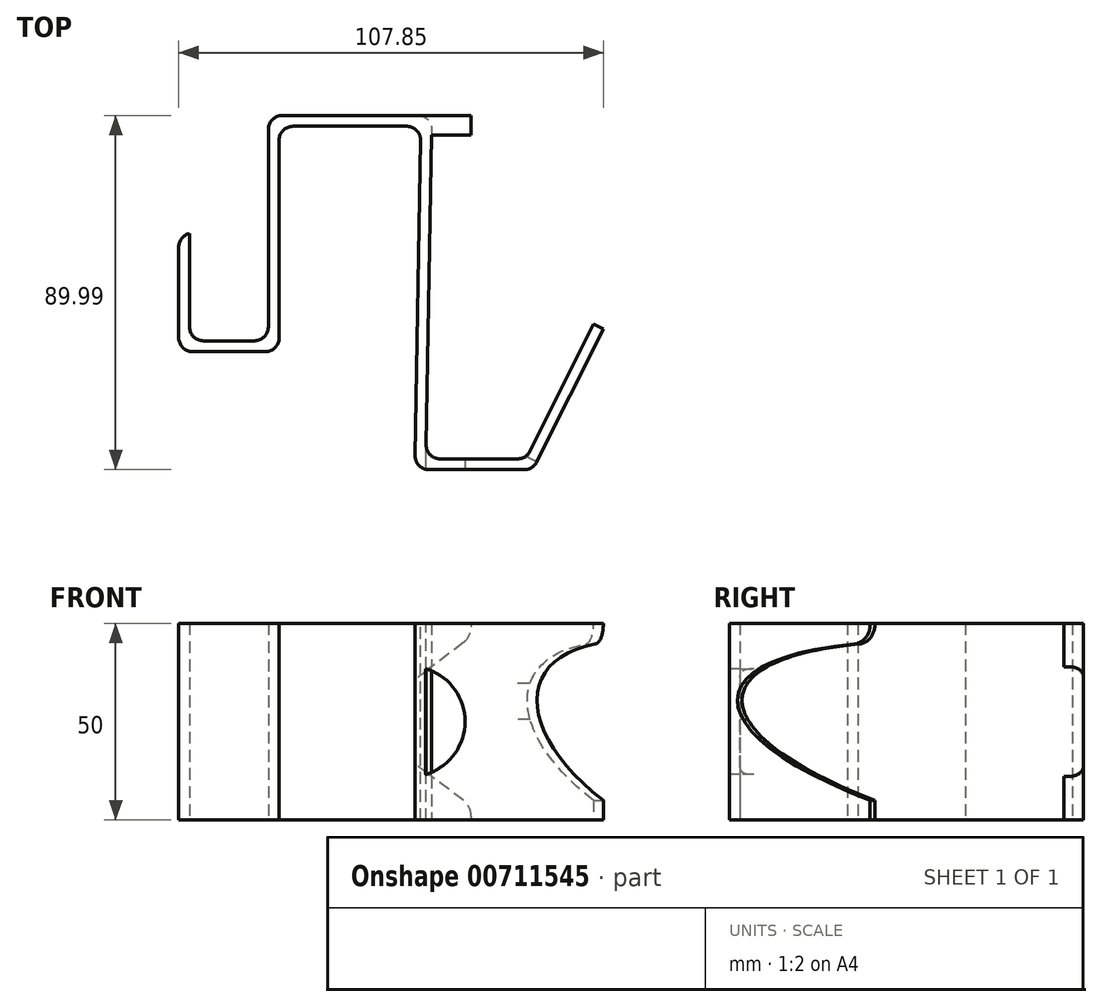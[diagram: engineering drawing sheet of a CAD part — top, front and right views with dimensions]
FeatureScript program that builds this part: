
annotation { "Feature Type Name" : "Feature", "Feature Type Description" : "" }
export const myFeature = defineFeature(function(context is Context, id is Id, definition is map)
    precondition{}
    {
        {
            var Q0;
            Q0=qCreatedBy(makeId("Top.planeOp"),FACE);
            var sketch = newSketch(context, id + "F0", { "sketchPlane" : qUnion([Q0])});
            skLineSegment(sketch, "E0.bottom", {"start": v(-19.06, 66.3) * mm, "end": v(19.74, 66.3) * mm});
            skLineSegment(sketch, "E0.top", {"start": v(-19.06, 6.3) * mm, "end": v(-16.3, 6.3) * mm});
            skLineSegment(sketch, "E0.left", {"start": v(-19.06, 66.3) * mm, "end": v(-19.06, 6.3) * mm});
            skLineSegment(sketch, "E1", {"start": v(-16.3, 6.3) * mm, "end": v(-16.3, 63.56) * mm});
            skLineSegment(sketch, "E2", {"start": v(-16.3, 63.56) * mm, "end": v(19.7, 63.56) * mm});
            skLineSegment(sketch, "E3", {"start": v(-19.06, 6.3) * mm, "end": v(-41.8, 6.3) * mm});
            skLineSegment(sketch, "E4", {"start": v(-41.8, 6.3) * mm, "end": v(-41.8, 36.3) * mm});
            skLineSegment(sketch, "E5", {"start": v(-41.8, 36.3) * mm, "end": v(-39.06, 36.3) * mm});
            skLineSegment(sketch, "E6", {"start": v(-39.06, 36.3) * mm, "end": v(-39.06, 9.06) * mm});
            skLineSegment(sketch, "E7", {"start": v(-39.06, 9.06) * mm, "end": v(-19.06, 9.06) * mm});
            skLineSegment(sketch, "E8", {"start": v(19.74, 66.3) * mm, "end": v(18.18, -23.68) * mm});
            skLineSegment(sketch, "E9", {"start": v(18.18, -23.68) * mm, "end": v(48.18, -23.68) * mm});
            skLineSegment(sketch, "E10", {"start": v(48.18, -23.68) * mm, "end": v(66.04, 12.11) * mm});
            skLineSegment(sketch, "E11", {"start": v(66.04, 12.11) * mm, "end": v(63.58, 13.34) * mm});
            skLineSegment(sketch, "E12", {"start": v(63.58, 13.34) * mm, "end": v(46.48, -20.93) * mm});
            skLineSegment(sketch, "E13", {"start": v(46.48, -20.93) * mm, "end": v(20.97, -20.93) * mm});
            skLineSegment(sketch, "E14", {"start": v(20.97, -20.93) * mm, "end": v(22.5, 66.3) * mm});
            skLineSegment(sketch, "E15", {"start": v(22.5, 66.3) * mm, "end": v(19.74, 66.3) * mm});
            skSolve(sketch);
        }
        {
            var Q0;
            {var subQ0=sQuery(id+"F0.wireOp",EDGE,"E3");Q0=makeQuery(id+"F0.imprint","IMPRINT",FACE,{"disambiguationData":[TD([[makeQuery(id+"F0.imprint","IMPRINT",EDGE,{"derivedFrom":subQ0}),-1.0]])]});}
            var Q1;
            {var subQ3=sQuery(id+"F0.wireOp",EDGE,"E0.bottom");Q1=makeQuery(id+"F0.imprint","IMPRINT",FACE,{"disambiguationData":[TD([[makeQuery(id+"F0.imprint","IMPRINT",EDGE,{"derivedFrom":subQ3}),-1.0]])]});}
            var Q2;
            {var subQ0=sQuery(id+"F0.wireOp",EDGE,"E9");Q2=makeQuery(id+"F0.imprint","IMPRINT",FACE,{"disambiguationData":[TD([[makeQuery(id+"F0.imprint","IMPRINT",EDGE,{"derivedFrom":subQ0}),1.0]])]});}
            extrude(context, id + "F1", {"entities" : qUnion([Q0, Q1, Q2]), "depth" : 50 * mm, "offsetDistance" : 25 * mm});
        }
        {
            var Q0;
            Q0=makeQuery(id+"F1.opExtrude","SWEPT_FACE",FACE,{"disambiguationData":[OSD([sQuery(id+"F0.wireOp",EDGE,"E10")])]});
            var sketch = newSketch(context, id + "F2", { "sketchPlane" : qUnion([Q0])});
            skLineSegment(sketch, "E16.0.0", {"start": v(0.33, 0) * mm, "end": v(40.33, 0) * mm});
            skLineSegment(sketch, "E16.0.1", {"start": v(40.33, 0) * mm, "end": v(40.33, 50) * mm});
            skLineSegment(sketch, "E16.0.2", {"start": v(40.33, 50) * mm, "end": v(0.33, 50) * mm});
            skLineSegment(sketch, "E16.0.3", {"start": v(0.33, 50) * mm, "end": v(0.33, 0) * mm});
            skPoint(sketch, "E17", {"position": v(40.33, 5) * mm});
            skPoint(sketch, "E18", {"position": v(40.33, 45) * mm});
            skPoint(sketch, "E19", {"position": v(0.33, 35) * mm});
            skFitSpline(sketch, "E20", {"points": [v(40.33, 5) * mm, v(40.33, 45) * mm], "startDerivative": vector(-149.65, 51.39) * mm, "endDerivative": vector(152.19, 8.84) * mm});
            skSolve(sketch);
        }
        {
            var Q0;
            {var subQ0=sQuery(id+"F2.wireOp",EDGE,"E20");Q0=makeQuery(id+"F2.imprint","IMPRINT",FACE,{"disambiguationData":[TD([[makeQuery(id+"F2.imprint","IMPRINT",EDGE,{"derivedFrom":subQ0}),-1.0]])]});}
            extrude(context, id + "F3", {"entities" : qUnion([Q0]), "operationType" : NewBodyOperationType.REMOVE, "oppositeDirection" : true, "depth" : 25 * mm, "offsetDistance" : 25 * mm});
        }
        {
            var Q0;
            {var subQ0=sQuery(id+"F2.wireOp",EDGE,"E20");var subQ1=sQuery(id+"F2.wireOp",EDGE,"E16.0.1");Q0=makeQuery(id+"F3.boolean.opBoolean","COPY",EDGE,{"derivedFrom":makeQuery(id+"F3.opExtrude","SWEPT_EDGE",EDGE,{"disambiguationData":[OSD([subQ1,subQ0]),TDD([makeQuery(id+"F2.imprint","INTERSECT",VERTEX,{"disambiguationData":[OD(0.0)],"derivedFrom":[subQ1,subQ0]})])]})});}
            var Q1;
            {var subQ0=sQuery(id+"F2.wireOp",EDGE,"E20");var subQ1=sQuery(id+"F2.wireOp",EDGE,"E16.0.1");Q1=makeQuery(id+"F3.boolean.opBoolean","COPY",EDGE,{"derivedFrom":makeQuery(id+"F3.opExtrude","SWEPT_EDGE",EDGE,{"disambiguationData":[OSD([subQ1,subQ0]),TDD([makeQuery(id+"F2.imprint","INTERSECT",VERTEX,{"disambiguationData":[OD(1.0)],"derivedFrom":[subQ1,subQ0]})])]})});}
            fillet(context, id + "F4", {"entities" : qUnion([Q0, Q1]), "radius" : 5 * mm, "tangentPropagation" : true, "allowEdgeOverflow" : false});
        }
        {
            var Q0;
            Q0=makeQuery(id+"F1.opExtrude","SWEPT_FACE",FACE,{"disambiguationData":[OSD([sQuery(id+"F0.wireOp",EDGE,"E0.bottom"),sQuery(id+"F0.wireOp",EDGE,"E15")])]});
            var sketch = newSketch(context, id + "F5", { "sketchPlane" : qUnion([Q0])});
            skLineSegment(sketch, "E21.0.0", {"start": v(-22.5, 0) * mm, "end": v(19.06, 0) * mm});
            skLineSegment(sketch, "E21.0.1", {"start": v(19.06, 0) * mm, "end": v(19.06, 50) * mm});
            skLineSegment(sketch, "E21.0.2", {"start": v(19.06, 50) * mm, "end": v(-22.5, 50) * mm});
            skLineSegment(sketch, "E22.bottom", {"start": v(-22.5, 50) * mm, "end": v(-32.5, 50) * mm});
            skLineSegment(sketch, "E22.top", {"start": v(-22.5, 0) * mm, "end": v(-32.5, 0) * mm});
            skLineSegment(sketch, "E22.right", {"start": v(-32.5, 50) * mm, "end": v(-32.5, 0) * mm});
            skLineSegment(sketch, "E23", {"start": v(-32.5, 46.57) * mm, "end": v(-21.5, 38.21) * mm});
            skPoint(sketch, "E24", {"position": v(19.06, 25) * mm});
            skPoint(sketch, "E25", {"position": v(-22.5, 25) * mm});
            skLineSegment(sketch, "E26", {"start": v(19.06, 25) * mm, "end": v(-22.5, 25) * mm, "construction": true});
            skLineSegment(sketch, "E27.MirrorCS", {"start": v(-32.5, 3.43) * mm, "end": v(-21.5, 11.79) * mm});
            skLineSegment(sketch, "E28", {"start": v(-21.5, 50) * mm, "end": v(-21.5, 0) * mm});
            skPoint(sketch, "E29.orphan", {"position": v(-32.5, 3.43) * mm});
            skPoint(sketch, "E30.orphan", {"position": v(-22.5, 38.97) * mm});
            skPoint(sketch, "E31.orphan", {"position": v(-22.5, 11.03) * mm});
            skSolve(sketch);
        }
        {
            var Q0;
            {var subQ0=sQuery(id+"F5.wireOp",EDGE,"E22.bottom");Q0=makeQuery(id+"F5.imprint","IMPRINT",FACE,{"disambiguationData":[TD([[makeQuery(id+"F5.imprint","IMPRINT",EDGE,{"derivedFrom":subQ0}),1.0]])]});}
            var Q1;
            {var subQ0=sQuery(id+"F5.wireOp",EDGE,"E22.top");Q1=makeQuery(id+"F5.imprint","IMPRINT",FACE,{"disambiguationData":[TD([[makeQuery(id+"F5.imprint","IMPRINT",EDGE,{"derivedFrom":subQ0}),-1.0]])]});}
            var Q2;
            {var subQ3=sQuery(id+"F5.wireOp",EDGE,"E28");var subQ5=sQuery(id+"F5.wireOp",EDGE,"E23");var subQ6=makeQuery(id+"F5.imprint","INTERSECT",VERTEX,{"derivedFrom":[subQ5,subQ3]});Q2=makeQuery(id+"F5.imprint","IMPRINT",FACE,{"disambiguationData":[TD([[makeQuery(id+"F5.imprint","IMPRINT",EDGE,{"disambiguationData":[TD([[subQ6,1.0]])],"derivedFrom":subQ3}),-1.0]])]});}
            var Q3;
            {var subQ3=sQuery(id+"F5.wireOp",EDGE,"E28");var subQ5=sQuery(id+"F5.wireOp",EDGE,"E27.MirrorCS");var subQ6=makeQuery(id+"F5.imprint","INTERSECT",VERTEX,{"derivedFrom":[subQ5,subQ3]});Q3=makeQuery(id+"F5.imprint","IMPRINT",FACE,{"disambiguationData":[TD([[makeQuery(id+"F5.imprint","IMPRINT",EDGE,{"disambiguationData":[TD([[subQ6,-1.0]])],"derivedFrom":subQ3}),-1.0]])]});}
            extrude(context, id + "F6", {"entities" : qUnion([Q0, Q1, Q2, Q3]), "operationType" : NewBodyOperationType.ADD, "oppositeDirection" : true, "depth" : 5 * mm, "offsetDistance" : 25 * mm});
        }
        {
            var Q0;
            Q0=makeQuery(id+"F6.opExtrude","SWEPT_EDGE",EDGE,{"disambiguationData":[OSD([sQuery(id+"F5.wireOp",EDGE,"E22.right"),sQuery(id+"F5.wireOp",EDGE,"E27.MirrorCS")])]});
            var Q1;
            Q1=makeQuery(id+"F6.opExtrude","SWEPT_EDGE",EDGE,{"disambiguationData":[OSD([sQuery(id+"F5.wireOp",EDGE,"E22.right"),sQuery(id+"F5.wireOp",EDGE,"E23")])]});
            fillet(context, id + "F7", {"entities" : qUnion([Q0, Q1]), "radius" : 5 * mm, "tangentPropagation" : true, "allowEdgeOverflow" : false});
        }
        {
            var Q0;
            Q0=makeQuery(id+"F1.opExtrude","SWEPT_FACE",FACE,{"disambiguationData":[OSD([sQuery(id+"F0.wireOp",EDGE,"E9")])]});
            var sketch = newSketch(context, id + "F8", { "sketchPlane" : qUnion([Q0])});
            skLineSegment(sketch, "E32.0.0", {"start": v(18.18, 0) * mm, "end": v(48.18, 0) * mm});
            skLineSegment(sketch, "E32.0.1", {"start": v(48.18, 0) * mm, "end": v(48.18, 50) * mm});
            skLineSegment(sketch, "E32.0.2", {"start": v(48.18, 50) * mm, "end": v(18.18, 50) * mm});
            skLineSegment(sketch, "E32.0.3", {"start": v(18.18, 50) * mm, "end": v(18.18, 0) * mm});
            skLineSegment(sketch, "E33.bottom", {"start": v(48.18, 50) * mm, "end": v(20.93, 50) * mm});
            skLineSegment(sketch, "E33.top", {"start": v(48.18, 0) * mm, "end": v(20.93, 0) * mm});
            skLineSegment(sketch, "E33.left", {"start": v(48.18, 50) * mm, "end": v(48.18, 0) * mm});
            skLineSegment(sketch, "E33.right", {"start": v(20.93, 50) * mm, "end": v(20.93, 0) * mm});
            skArc(sketch, "E34", {"start": v(20.93, 11.55) * mm, "mid": v(30.9, 25) * mm, "end": v(20.93, 38.45) * mm});
            skPoint(sketch, "E35", {"position": v(20.93, 25) * mm});
            skSolve(sketch);
        }
        {
            var Q0;
            {var subQ0=sQuery(id+"F8.wireOp",EDGE,"E34");Q0=makeQuery(id+"F8.imprint","IMPRINT",FACE,{"disambiguationData":[TD([[makeQuery(id+"F8.imprint","IMPRINT",EDGE,{"derivedFrom":subQ0}),1.0]])]});}
            extrude(context, id + "F9", {"entities" : qUnion([Q0]), "operationType" : NewBodyOperationType.REMOVE, "oppositeDirection" : true, "depth" : 2.75 * mm, "offsetDistance" : 25 * mm});
        }
        {
            var Q0;
            Q0=makeQuery(id+"F1.opExtrude","SWEPT_EDGE",EDGE,{"disambiguationData":[OSD([sQuery(id+"F0.wireOp",EDGE,"E0.bottom"),sQuery(id+"F0.wireOp",EDGE,"E0.left")])]});
            var Q1;
            Q1=makeQuery(id+"F1.opExtrude","SWEPT_EDGE",EDGE,{"disambiguationData":[OSD([sQuery(id+"F0.wireOp",EDGE,"E4"),sQuery(id+"F0.wireOp",EDGE,"E5")])]});
            var Q2;
            Q2=makeQuery(id+"F1.opExtrude","SWEPT_EDGE",EDGE,{"disambiguationData":[OSD([sQuery(id+"F0.wireOp",EDGE,"E3"),sQuery(id+"F0.wireOp",EDGE,"E4")])]});
            var Q3;
            Q3=makeQuery(id+"F1.opExtrude","SWEPT_EDGE",EDGE,{"disambiguationData":[OSD([sQuery(id+"F0.wireOp",EDGE,"E0.top"),sQuery(id+"F0.wireOp",EDGE,"E1")])]});
            var Q4;
            Q4=makeQuery(id+"F1.opExtrude","SWEPT_EDGE",EDGE,{"disambiguationData":[OSD([sQuery(id+"F0.wireOp",EDGE,"E8"),sQuery(id+"F0.wireOp",EDGE,"E9")])]});
            var Q5;
            Q5=makeQuery(id+"F1.opExtrude","SWEPT_EDGE",EDGE,{"disambiguationData":[OSD([sQuery(id+"F0.wireOp",EDGE,"E9"),sQuery(id+"F0.wireOp",EDGE,"E10")])]});
            var Q6;
            Q6=makeQuery(id+"F1.opExtrude","SWEPT_EDGE",EDGE,{"disambiguationData":[OSD([sQuery(id+"F0.wireOp",EDGE,"E2"),sQuery(id+"F0.wireOp",EDGE,"E8")])]});
            var Q7;
            Q7=makeQuery(id+"F1.opExtrude","SWEPT_EDGE",EDGE,{"disambiguationData":[OSD([sQuery(id+"F0.wireOp",EDGE,"E1"),sQuery(id+"F0.wireOp",EDGE,"E2")])]});
            var Q8;
            Q8=makeQuery(id+"F1.opExtrude","SWEPT_EDGE",EDGE,{"disambiguationData":[OSD([sQuery(id+"F0.wireOp",EDGE,"E14"),sQuery(id+"F0.wireOp",EDGE,"E15")])]});
            var Q9;
            {var subQ1=sQuery(id+"F0.wireOp",EDGE,"E14");var subQ2=makeQuery(id+"F1.opExtrude","SWEPT_FACE",FACE,{"disambiguationData":[OSD([subQ1])]});var subQ3=sQuery(id+"F0.wireOp",EDGE,"E13");var subQ4=makeQuery(id+"F1.opExtrude","SWEPT_FACE",FACE,{"disambiguationData":[OSD([subQ3])]});Q9=makeQuery(id+"F9.boolean.opBoolean","SPLIT",EDGE,{"disambiguationData":[topologyDisambiguationEdgeConnected([subQ4,subQ2]),TD([makeQuery(id+"F6.opExtrude","SWEPT_FACE",FACE,{"disambiguationData":[OSD([sQuery(id+"F5.wireOp",EDGE,"E21.0.0"),sQuery(id+"F5.wireOp",EDGE,"E22.top")])]})])],"derivedFrom":makeQuery(id+"F1.opExtrude","SWEPT_EDGE",EDGE,{"disambiguationData":[OSD([subQ3,subQ1])]})});}
            var Q10;
            {var subQ0=sQuery(id+"F0.wireOp",EDGE,"E14");var subQ1=makeQuery(id+"F1.opExtrude","SWEPT_FACE",FACE,{"disambiguationData":[OSD([subQ0])]});var subQ2=sQuery(id+"F0.wireOp",EDGE,"E13");var subQ3=makeQuery(id+"F1.opExtrude","SWEPT_FACE",FACE,{"disambiguationData":[OSD([subQ2])]});Q10=makeQuery(id+"F9.boolean.opBoolean","SPLIT",EDGE,{"disambiguationData":[topologyDisambiguationEdgeConnected([subQ3,subQ1]),TD([makeQuery(id+"F6.opExtrude","SWEPT_FACE",FACE,{"disambiguationData":[OSD([sQuery(id+"F5.wireOp",EDGE,"E21.0.2"),sQuery(id+"F5.wireOp",EDGE,"E22.bottom")])]})])],"derivedFrom":makeQuery(id+"F1.opExtrude","SWEPT_EDGE",EDGE,{"disambiguationData":[OSD([subQ2,subQ0])]})});}
            var Q11;
            Q11=makeQuery(id+"F1.opExtrude","SWEPT_EDGE",EDGE,{"disambiguationData":[OSD([sQuery(id+"F0.wireOp",EDGE,"E12"),sQuery(id+"F0.wireOp",EDGE,"E13")])]});
            var Q12;
            Q12=makeQuery(id+"F1.opExtrude","SWEPT_EDGE",EDGE,{"disambiguationData":[OSD([sQuery(id+"F0.wireOp",EDGE,"E0.left"),sQuery(id+"F0.wireOp",EDGE,"E7")])]});
            var Q13;
            Q13=makeQuery(id+"F1.opExtrude","SWEPT_EDGE",EDGE,{"disambiguationData":[OSD([sQuery(id+"F0.wireOp",EDGE,"E6"),sQuery(id+"F0.wireOp",EDGE,"E7")])]});
            fillet(context, id + "F10", {"entities" : qUnion([Q0, Q1, Q2, Q3, Q4, Q5, Q6, Q7, Q8, Q9, Q10, Q11, Q12, Q13]), "radius" : 3.5 * mm, "tangentPropagation" : true, "allowEdgeOverflow" : false});
        }
    });
